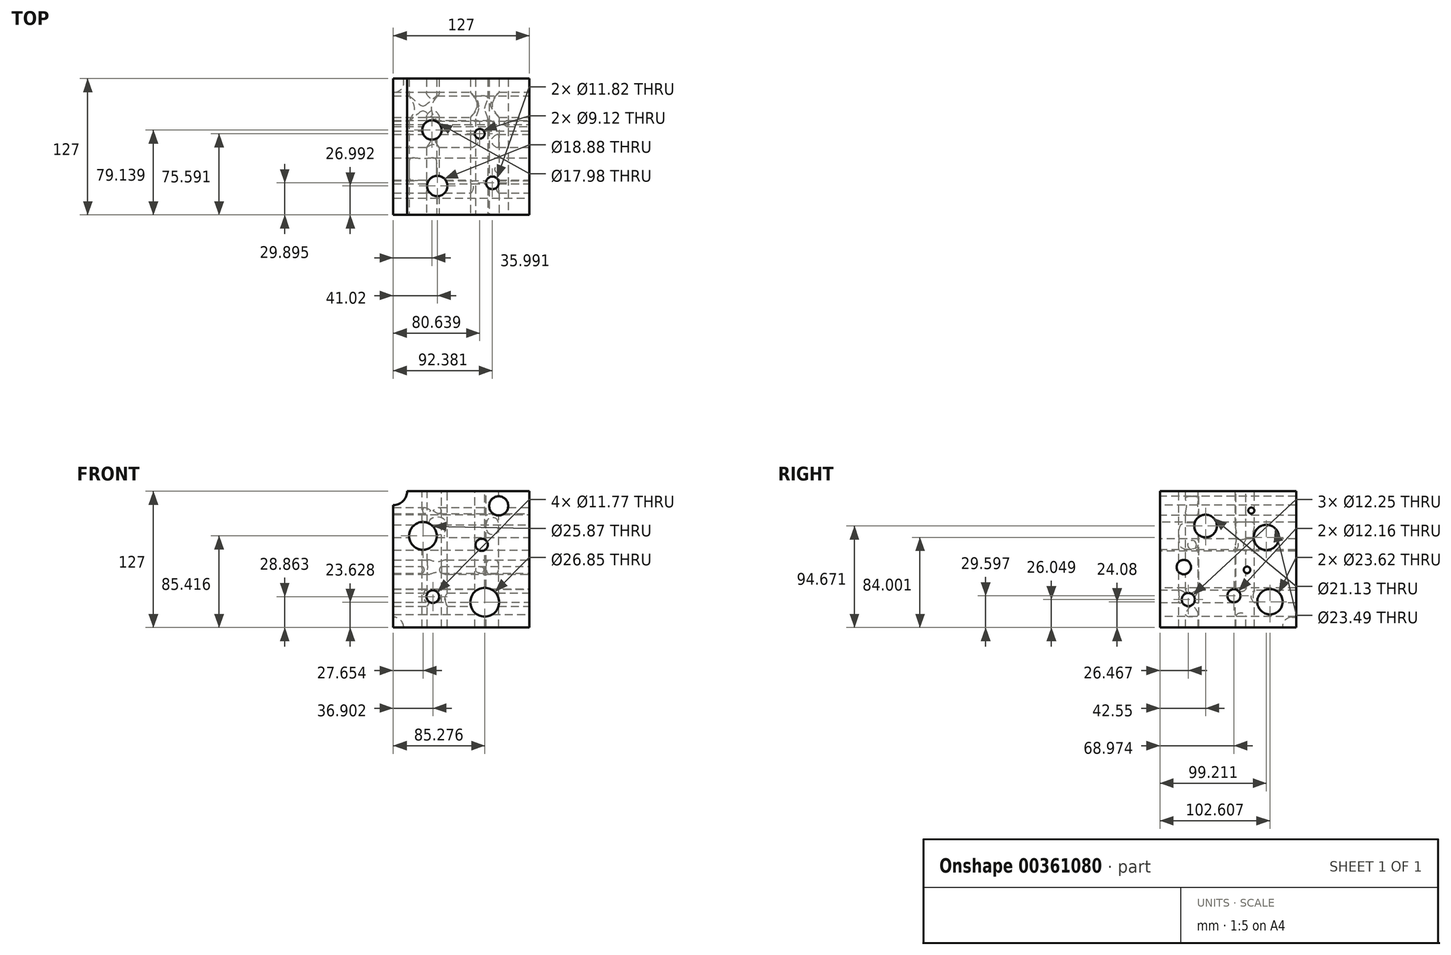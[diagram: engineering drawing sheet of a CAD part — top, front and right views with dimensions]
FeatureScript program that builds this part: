
annotation { "Feature Type Name" : "Feature", "Feature Type Description" : "" }
export const myFeature = defineFeature(function(context is Context, id is Id, definition is map)
    precondition{}
    {
        {
            var Q0;
            Q0=qCreatedBy(makeId("Front.planeOp"),FACE);
            var sketch = newSketch(context, id + "F0", { "sketchPlane" : qUnion([Q0])});
            skLineSegment(sketch, "E0.bottom", {"start": v(67, 61.63) * mm, "end": v(-60, 61.63) * mm});
            skLineSegment(sketch, "E0.top", {"start": v(67, -65.37) * mm, "end": v(-60, -65.37) * mm});
            skLineSegment(sketch, "E0.left", {"start": v(67, 61.63) * mm, "end": v(67, -65.37) * mm});
            skLineSegment(sketch, "E0.right", {"start": v(-60, 61.63) * mm, "end": v(-60, -65.37) * mm});
            skSolve(sketch);
        }
        {
            var Q0;
            Q0=makeQuery(id+"F0.imprint","IMPRINT",FACE,{"disambiguationData":[TD([[makeQuery(id+"F0.imprint","IMPRINT",EDGE,{"derivedFrom":sQuery(id+"F0.wireOp",EDGE,"E0.bottom")}),1.0]])]});
            extrude(context, id + "F1", {"entities" : qUnion([Q0]), "depth" : 127 * mm});
        }
        {
            var Q0;
            Q0=makeQuery(id+"F1.opExtrude","CAP_FACE",FACE,{"disambiguationData":[OSD([sQuery(id+"F0.wireOp",EDGE,"E0.bottom"),sQuery(id+"F0.wireOp",EDGE,"E0.top"),sQuery(id+"F0.wireOp",EDGE,"E0.left"),sQuery(id+"F0.wireOp",EDGE,"E0.right")])],"isStart":false});
            var sketch = newSketch(context, id + "F2", { "sketchPlane" : qUnion([Q0])});
            skCircle(sketch, "E1", {"center": v(-23.1, -36.5) * mm, "radius": 5.89 * mm});
            skCircle(sketch, "E2", {"center": v(22.4, 11.74) * mm, "radius": 5.7 * mm});
            skCircle(sketch, "E3", {"center": v(25.28, -41.74) * mm, "radius": 13.43 * mm});
            skCircle(sketch, "E4", {"center": v(-32.35, 20.05) * mm, "radius": 12.94 * mm});
            skCircle(sketch, "E5", {"center": v(38.28, 48.04) * mm, "radius": 8.88 * mm});
            skCircle(sketch, "E6", {"center": v(-60, 61.63) * mm, "radius": 12.9 * mm});
            skSolve(sketch);
        }
        {
            var Q0;
            Q0=makeQuery(id+"F2.imprint","IMPRINT",FACE,{"disambiguationData":[TD([[makeQuery(id+"F2.imprint","IMPRINT",EDGE,{"derivedFrom":sQuery(id+"F2.wireOp",EDGE,"E4")}),1.0]])]});
            var Q1;
            Q1=makeQuery(id+"F2.imprint","IMPRINT",FACE,{"disambiguationData":[TD([[makeQuery(id+"F2.imprint","IMPRINT",EDGE,{"derivedFrom":sQuery(id+"F2.wireOp",EDGE,"E2")}),1.0]])]});
            var Q2;
            Q2=makeQuery(id+"F2.imprint","IMPRINT",FACE,{"disambiguationData":[TD([[makeQuery(id+"F2.imprint","IMPRINT",EDGE,{"derivedFrom":sQuery(id+"F2.wireOp",EDGE,"E5")}),1.0]])]});
            var Q3;
            Q3=makeQuery(id+"F2.imprint","IMPRINT",FACE,{"disambiguationData":[TD([[makeQuery(id+"F2.imprint","IMPRINT",EDGE,{"derivedFrom":sQuery(id+"F2.wireOp",EDGE,"E3")}),1.0]])]});
            var Q4;
            Q4=makeQuery(id+"F2.imprint","IMPRINT",FACE,{"disambiguationData":[TD([[makeQuery(id+"F2.imprint","IMPRINT",EDGE,{"derivedFrom":sQuery(id+"F2.wireOp",EDGE,"E1")}),1.0]])]});
            var Q5;
            {var subQ0=sQuery(id+"F2.wireOp",EDGE,"E6");var subQ1=makeQuery(id+"F1.opExtrude","CAP_EDGE",EDGE,{"disambiguationData":[OSD([sQuery(id+"F0.wireOp",EDGE,"E0.bottom")])],"isStart":false});var subQ2=makeQuery(id+"F2.imprint","INTERSECT",VERTEX,{"derivedFrom":[subQ1,subQ0]});Q5=makeQuery(id+"F2.imprint","IMPRINT",FACE,{"disambiguationData":[TD([[makeQuery(id+"F2.imprint","IMPRINT",EDGE,{"disambiguationData":[TD([[subQ2,-1.0]])],"derivedFrom":subQ0}),1.0]])]});}
            var Q6;
            {var subQ0=sQuery(id+"F2.wireOp",EDGE,"E6");var subQ1=makeQuery(id+"F1.opExtrude","CAP_EDGE",EDGE,{"disambiguationData":[OSD([sQuery(id+"F0.wireOp",EDGE,"E0.bottom")])],"isStart":false});var subQ2=makeQuery(id+"F2.imprint","INTERSECT",VERTEX,{"derivedFrom":[subQ1,subQ0]});Q6=makeQuery(id+"F2.imprint","IMPRINT",FACE,{"disambiguationData":[TD([[makeQuery(id+"F2.imprint","IMPRINT",EDGE,{"disambiguationData":[TD([[subQ2,1.0]])],"derivedFrom":subQ0}),1.0]])]});}
            extrude(context, id + "F3", {"entities" : qUnion([Q0, Q1, Q2, Q3, Q4, Q5, Q6]), "operationType" : NewBodyOperationType.REMOVE, "oppositeDirection" : true, "depth" : 127 * mm});
        }
        {
            var Q0;
            Q0=makeQuery(id+"F1.opExtrude","SWEPT_FACE",FACE,{"disambiguationData":[OSD([sQuery(id+"F0.wireOp",EDGE,"E0.bottom")])]});
            var sketch = newSketch(context, id + "F4", { "sketchPlane" : qUnion([Q0])});
            skCircle(sketch, "E7", {"center": v(-18.98, -100) * mm, "radius": 9.44 * mm});
            skCircle(sketch, "E8", {"center": v(32.38, -97.1) * mm, "radius": 5.91 * mm});
            skCircle(sketch, "E9", {"center": v(-24, -47.86) * mm, "radius": 9 * mm});
            skCircle(sketch, "E10", {"center": v(20.64, -51.4) * mm, "radius": 4.56 * mm});
            skSolve(sketch);
        }
        {
            var Q0;
            Q0=makeQuery(id+"F4.imprint","IMPRINT",FACE,{"disambiguationData":[TD([[makeQuery(id+"F4.imprint","IMPRINT",EDGE,{"derivedFrom":sQuery(id+"F4.wireOp",EDGE,"E7")}),1.0]])]});
            var Q1;
            Q1=makeQuery(id+"F4.imprint","IMPRINT",FACE,{"disambiguationData":[TD([[makeQuery(id+"F4.imprint","IMPRINT",EDGE,{"derivedFrom":sQuery(id+"F4.wireOp",EDGE,"E8")}),1.0]])]});
            var Q2;
            Q2=makeQuery(id+"F4.imprint","IMPRINT",FACE,{"disambiguationData":[TD([[makeQuery(id+"F4.imprint","IMPRINT",EDGE,{"derivedFrom":sQuery(id+"F4.wireOp",EDGE,"E10")}),1.0]])]});
            var Q3;
            Q3=makeQuery(id+"F4.imprint","IMPRINT",FACE,{"disambiguationData":[TD([[makeQuery(id+"F4.imprint","IMPRINT",EDGE,{"derivedFrom":sQuery(id+"F4.wireOp",EDGE,"E9")}),1.0]])]});
            extrude(context, id + "F5", {"entities" : qUnion([Q0, Q1, Q2, Q3]), "operationType" : NewBodyOperationType.REMOVE, "oppositeDirection" : true, "depth" : 127 * mm});
        }
        {
            var Q0;
            Q0=makeQuery(id+"F1.opExtrude","SWEPT_FACE",FACE,{"disambiguationData":[OSD([sQuery(id+"F0.wireOp",EDGE,"E0.left")])]});
            var sketch = newSketch(context, id + "F6", { "sketchPlane" : qUnion([Q0])});
            skCircle(sketch, "E11", {"center": v(-41.8, 43.64) * mm, "radius": 2.83 * mm});
            skCircle(sketch, "E12", {"center": v(-84.45, 29.3) * mm, "radius": 10.57 * mm});
            skCircle(sketch, "E13", {"center": v(-45.77, -11.6) * mm, "radius": 3.08 * mm});
            skCircle(sketch, "E14", {"center": v(-27.79, 18.63) * mm, "radius": 11.74 * mm});
            skCircle(sketch, "E15", {"center": v(-104.72, -8.99) * mm, "radius": 6.73 * mm});
            skCircle(sketch, "E16", {"center": v(-58.03, -35.77) * mm, "radius": 6.08 * mm});
            skCircle(sketch, "E17", {"center": v(-24.4, -41.29) * mm, "radius": 11.8 * mm});
            skCircle(sketch, "E18", {"center": v(-100.53, -39.32) * mm, "radius": 6.12 * mm});
            skSolve(sketch);
        }
        {
            var Q0;
            Q0=makeQuery(id+"F6.imprint","IMPRINT",FACE,{"disambiguationData":[TD([[makeQuery(id+"F6.imprint","IMPRINT",EDGE,{"derivedFrom":sQuery(id+"F6.wireOp",EDGE,"E14")}),1.0]])]});
            var Q1;
            Q1=makeQuery(id+"F6.imprint","IMPRINT",FACE,{"disambiguationData":[TD([[makeQuery(id+"F6.imprint","IMPRINT",EDGE,{"derivedFrom":sQuery(id+"F6.wireOp",EDGE,"E11")}),1.0]])]});
            var Q2;
            Q2=makeQuery(id+"F6.imprint","IMPRINT",FACE,{"disambiguationData":[TD([[makeQuery(id+"F6.imprint","IMPRINT",EDGE,{"derivedFrom":sQuery(id+"F6.wireOp",EDGE,"E12")}),1.0]])]});
            var Q3;
            Q3=makeQuery(id+"F6.imprint","IMPRINT",FACE,{"disambiguationData":[TD([[makeQuery(id+"F6.imprint","IMPRINT",EDGE,{"derivedFrom":sQuery(id+"F6.wireOp",EDGE,"E13")}),1.0]])]});
            var Q4;
            Q4=makeQuery(id+"F6.imprint","IMPRINT",FACE,{"disambiguationData":[TD([[makeQuery(id+"F6.imprint","IMPRINT",EDGE,{"derivedFrom":sQuery(id+"F6.wireOp",EDGE,"E16")}),1.0]])]});
            var Q5;
            Q5=makeQuery(id+"F6.imprint","IMPRINT",FACE,{"disambiguationData":[TD([[makeQuery(id+"F6.imprint","IMPRINT",EDGE,{"derivedFrom":sQuery(id+"F6.wireOp",EDGE,"E18")}),1.0]])]});
            var Q6;
            Q6=makeQuery(id+"F6.imprint","IMPRINT",FACE,{"disambiguationData":[TD([[makeQuery(id+"F6.imprint","IMPRINT",EDGE,{"derivedFrom":sQuery(id+"F6.wireOp",EDGE,"E15")}),1.0]])]});
            var Q7;
            Q7=makeQuery(id+"F6.imprint","IMPRINT",FACE,{"disambiguationData":[TD([[makeQuery(id+"F6.imprint","IMPRINT",EDGE,{"derivedFrom":sQuery(id+"F6.wireOp",EDGE,"E17")}),1.0]])]});
            extrude(context, id + "F7", {"entities" : qUnion([Q0, Q1, Q2, Q3, Q4, Q5, Q6, Q7]), "operationType" : NewBodyOperationType.REMOVE, "oppositeDirection" : true, "depth" : 127 * mm});
        }
        {
            var Q0;
            Q0=makeQuery(id+"F1.opExtrude","CAP_FACE",FACE,{"disambiguationData":[OSD([sQuery(id+"F0.wireOp",EDGE,"E0.bottom"),sQuery(id+"F0.wireOp",EDGE,"E0.top"),sQuery(id+"F0.wireOp",EDGE,"E0.left"),sQuery(id+"F0.wireOp",EDGE,"E0.right")])],"isStart":true});
            var sketch = newSketch(context, id + "F8", { "sketchPlane" : qUnion([Q0])});
            skPoint(sketch, "E19", {"position": v(60, -65.37) * mm});
            skSolve(sketch);
        }
        {
            var Q0;
            Q0=qCreatedBy(makeId("Front.planeOp"),FACE);
            var sketch = newSketch(context, id + "F9", { "sketchPlane" : qUnion([Q0])});
            skCircle(sketch, "E20", {"center": v(-60.35, -65.67) * mm, "radius": 10.13 * mm});
            skSolve(sketch);
        }
        {
            var Q0;
            Q0=makeQuery(id+"F9.imprint","IMPRINT",FACE,{"disambiguationData":[TD([[makeQuery(id+"F9.imprint","IMPRINT",EDGE,{"derivedFrom":sQuery(id+"F9.wireOp",EDGE,"E20")}),1.0]])]});
            extrude(context, id + "F10", {"entities" : qUnion([Q0]), "operationType" : NewBodyOperationType.REMOVE, "depth" : 12.7 * mm});
        }
        {
            var Q0;
            Q0=makeQuery(id+"F10.boolean.opBoolean","COPY",EDGE,{"derivedFrom":makeQuery(id+"F10.opExtrude","CAP_EDGE",EDGE,{"disambiguationData":[OSD([sQuery(id+"F9.wireOp",EDGE,"E20")])],"isStart":false})});
            fillet(context, id + "F11", {"entities" : qUnion([Q0]), "radius" : 8.9 * mm, "tangentPropagation" : true, "allowEdgeOverflow" : false});
        }
    });
